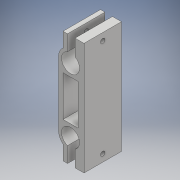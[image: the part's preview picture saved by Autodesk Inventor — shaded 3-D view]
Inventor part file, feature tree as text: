
AUTODESK INVENTOR PART (.ipt)
format: ipt  version: 2017 (Build 210142000, 142)  size: 181,760 bytes
history: native  units: mm
features: extrude x4, projected_geometry x4, sketch x3, other x1, hole x1
ambient origin geometry x8: Origin, YZ Plane, XZ Plane, XY Plane, X Axis, Y Axis, Z Axis, Center Point
bodies: Body1 (feature_tree)
feature tree (13):
  other  "Sólido1"
  extrude  "Extrusión1"  Depth=75.0mm
  extrude  "Extrusión3"  TaperAngle=0.0deg  [1 undecoded]
  extrude  "Extrusión5"  Depth=3.0mm
  hole  "Agujero1"  [1 undecoded]
  extrude  "Extrusión6"  Depth=3.0mm
  sketch  "Boceto2"  dims[d10=20.0mm d11=75.0mm]
  projected_geometry  "Contorno proyectado1"
  sketch  "Boceto4"  dims[d12=25.0mm d13=0.0mm d15=0.0mm]
  projected_geometry  "Contorno proyectado2"
  projected_geometry  "Contorno proyectado3"
  sketch  "Boceto5"  dims[d16=21.5mm d21=3.0mm d27=5.0mm d30=3.0mm d37=10.0mm d38=0.0mm d43=10.0mm d44=0.0mm d47=3.0mm d48=6.0mm d49=4.0mm d50=2.0mm d51=90.0deg d52=8.0mm d53=20.594885mm d54=2.0mm d55=5.0mm d56=6.0mm d57=2.0mm d58=7.0mm d59=10.0mm d60=3.0mm d61=10.0mm d62=0.0mm]
  projected_geometry  "Contorno proyectado4"
note: 2 required parameter values undecoded (feature->parameter linkage not recoverable at this tier; creation-order binding heuristic only, values carry confidence <= 0.55)
